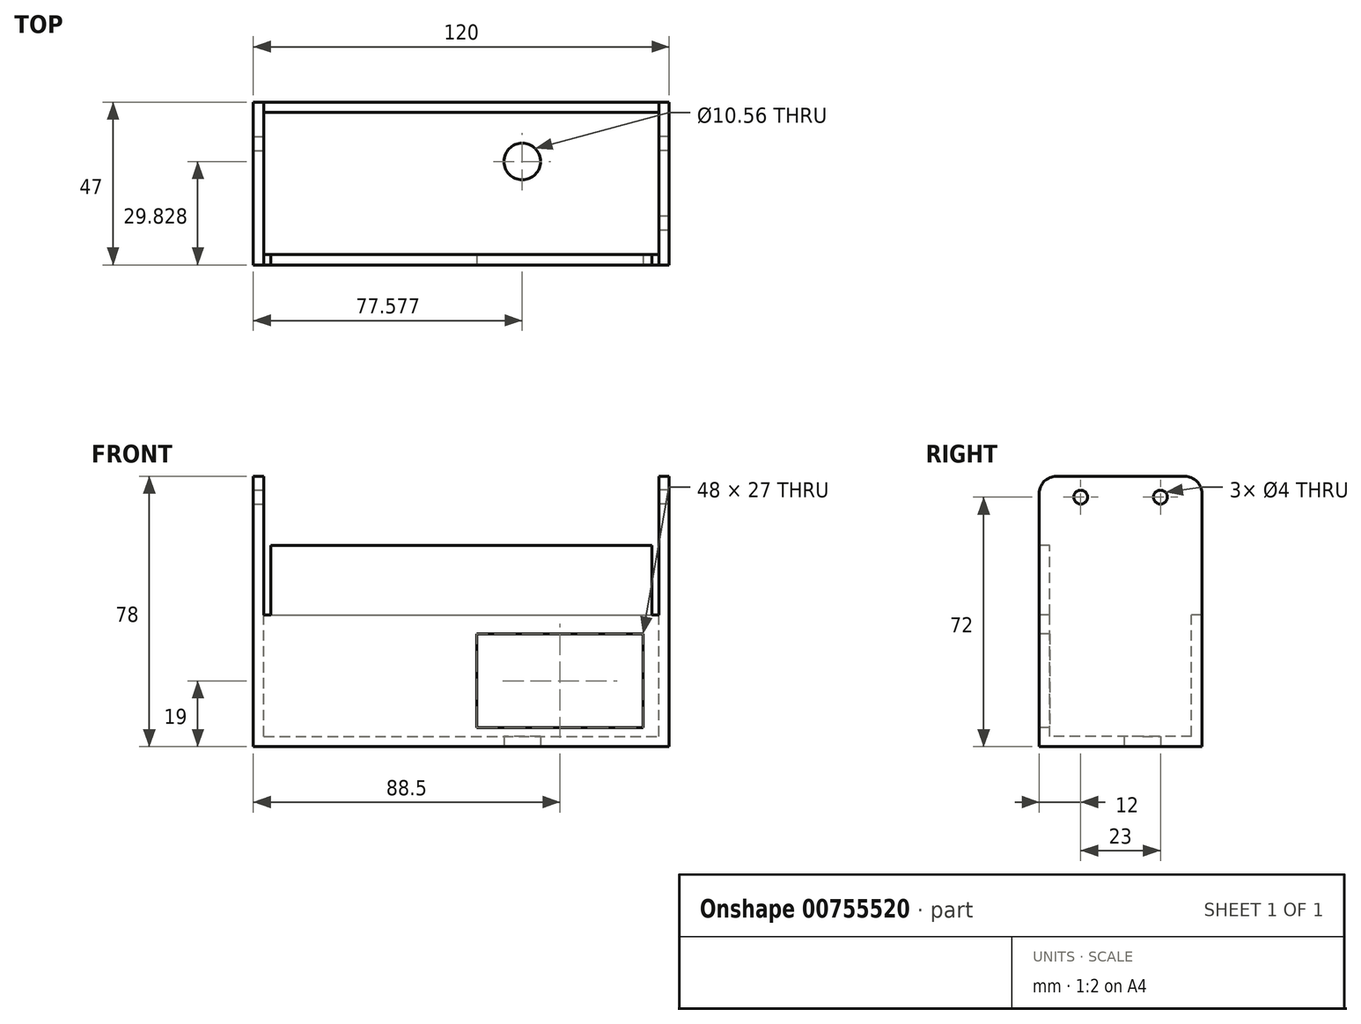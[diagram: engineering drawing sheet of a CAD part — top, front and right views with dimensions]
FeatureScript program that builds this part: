
annotation { "Feature Type Name" : "Feature", "Feature Type Description" : "" }
export const myFeature = defineFeature(function(context is Context, id is Id, definition is map)
    precondition{}
    {
        {
            assignVariable(context, id + "F0", {"name" : "wall", "anyValue" : 3});
        }
        {
            assignVariable(context, id + "F1", {"name" : "width", "anyValue" : 114});
        }
        {
            var Q0;
            Q0=qCreatedBy(makeId("Right.planeOp"),FACE);
            var sketch = newSketch(context, id + "F2", { "sketchPlane" : qUnion([Q0])});
            skLineSegment(sketch, "E0.bottom", {"start": v(17.5, 40) * mm, "end": v(-19.5, 40) * mm});
            skLineSegment(sketch, "E0.top", {"start": v(22.5, -38) * mm, "end": v(-24.5, -38) * mm});
            skLineSegment(sketch, "E0.left", {"start": v(22.5, 35) * mm, "end": v(22.5, -38) * mm});
            skLineSegment(sketch, "E0.right", {"start": v(-24.5, 35) * mm, "end": v(-24.5, -38) * mm});
            skCircle(sketch, "E1", {"center": v(10.5, 34) * mm, "radius": 2 * mm});
            skCircle(sketch, "E2", {"center": v(-12.5, 34) * mm, "radius": 2 * mm});
            skPoint(sketch, "E3.visualSharp", {"position": v(-24.5, 40) * mm});
            skArc(sketch, "E3.filletArc", {"start": v(-19.5, 40) * mm, "mid": v(-23.04, 38.54) * mm, "end": v(-24.5, 35) * mm});
            skPoint(sketch, "E4.visualSharp", {"position": v(22.5, 40) * mm});
            skArc(sketch, "E4.filletArc", {"start": v(22.5, 35) * mm, "mid": v(21.04, 38.54) * mm, "end": v(17.5, 40) * mm});
            skSolve(sketch);
        }
        {
            var Q0;
            Q0=qSketchRegion(id+"F2",true);
            extrude(context, id + "F3", {"entities" : qUnion([Q0]), "depth" : (getVariable(context, 'wall')) * mm, "offsetDistance" : 25 * mm});
        }
        {
            var Q0;
            Q0=qCreatedBy(makeId("Right.planeOp"),FACE);
            var sketch = newSketch(context, id + "F4", { "sketchPlane" : qUnion([Q0])});
            skLineSegment(sketch, "E5.bottom", {"start": v(22.5, -38) * mm, "end": v(-24.5, -38) * mm});
            skLineSegment(sketch, "E5.top", {"start": v(22.5, -35) * mm, "end": v(-24.5, -35) * mm});
            skLineSegment(sketch, "E5.left", {"start": v(22.5, -38) * mm, "end": v(22.5, -35) * mm});
            skLineSegment(sketch, "E5.right", {"start": v(-24.5, -38) * mm, "end": v(-24.5, -35) * mm});
            skLineSegment(sketch, "E6.bottom", {"start": v(-24.5, -38) * mm, "end": v(-21.5, -38) * mm});
            skLineSegment(sketch, "E6.top", {"start": v(-24.5, 0) * mm, "end": v(-21.5, 0) * mm});
            skLineSegment(sketch, "E6.left", {"start": v(-24.5, -38) * mm, "end": v(-24.5, 0) * mm});
            skLineSegment(sketch, "E6.right", {"start": v(-21.5, -38) * mm, "end": v(-21.5, 0) * mm});
            skLineSegment(sketch, "E7.bottom", {"start": v(22.5, -38) * mm, "end": v(19.5, -38) * mm});
            skLineSegment(sketch, "E7.top", {"start": v(22.5, 0) * mm, "end": v(19.5, 0) * mm});
            skLineSegment(sketch, "E7.left", {"start": v(22.5, -38) * mm, "end": v(22.5, 0) * mm});
            skLineSegment(sketch, "E7.right", {"start": v(19.5, -38) * mm, "end": v(19.5, 0) * mm});
            skSolve(sketch);
        }
        {
            var Q0;
            {var subQ0=sQuery(id+"F4.wireOp",EDGE,"E5.right");var subQ1=sQuery(id+"F4.wireOp",EDGE,"E5.bottom");var subQ9=sQuery(id+"F4.wireOp",EDGE,"E7.right");var subQ10=makeQuery(id+"F4.imprint","INTERSECT",VERTEX,{"derivedFrom":[subQ1,subQ9]});var subQ14=sQuery(id+"F4.wireOp",EDGE,"E5.left");var subQ16=sQuery(id+"F4.wireOp",EDGE,"E7.top");var subQ17=sQuery(id+"F4.wireOp",EDGE,"E6.top");Q0=qUnion([makeQuery(id+"F4.imprint","IMPRINT",FACE,{"disambiguationData":[TD([[makeQuery(id+"F4.imprint","IMPRINT",EDGE,{"derivedFrom":subQ17}),-1.0]])]}),makeQuery(id+"F4.imprint","IMPRINT",FACE,{"disambiguationData":[TD([[makeQuery(id+"F4.imprint","IMPRINT",EDGE,{"derivedFrom":subQ14}),1.0]])]}),makeQuery(id+"F4.imprint","IMPRINT",FACE,{"disambiguationData":[TD([[makeQuery(id+"F4.imprint","IMPRINT",EDGE,{"derivedFrom":subQ16}),1.0]])]}),makeQuery(id+"F4.imprint","IMPRINT",FACE,{"disambiguationData":[TD([[makeQuery(id+"F4.imprint","IMPRINT",EDGE,{"disambiguationData":[TD([[subQ10,-1.0]])],"derivedFrom":subQ1}),-1.0]])]}),makeQuery(id+"F4.imprint","IMPRINT",FACE,{"disambiguationData":[TD([[makeQuery(id+"F4.imprint","IMPRINT",EDGE,{"derivedFrom":subQ0}),-1.0]])]})]);}
            extrude(context, id + "F5", {"entities" : qUnion([Q0]), "operationType" : NewBodyOperationType.ADD, "oppositeDirection" : true, "depth" : (getVariable(context, 'width')) * mm, "offsetDistance" : 25 * mm});
        }
        {
            var Q0;
            Q0=makeQuery(id+"F5.opExtrude","CAP_FACE",FACE,{"disambiguationData":[OSD([sQuery(id+"F4.wireOp",EDGE,"E5.bottom"),sQuery(id+"F4.wireOp",EDGE,"E5.top"),sQuery(id+"F4.wireOp",EDGE,"E5.left"),sQuery(id+"F4.wireOp",EDGE,"E5.right"),sQuery(id+"F4.wireOp",EDGE,"E6.top"),sQuery(id+"F4.wireOp",EDGE,"E6.left"),sQuery(id+"F4.wireOp",EDGE,"E6.right"),sQuery(id+"F4.wireOp",EDGE,"E7.top"),sQuery(id+"F4.wireOp",EDGE,"E7.left"),sQuery(id+"F4.wireOp",EDGE,"E7.right")])],"isStart":false});
            var sketch = newSketch(context, id + "F6", { "sketchPlane" : qUnion([Q0])});
            skLineSegment(sketch, "E8.bottom", {"start": v(19.5, 40) * mm, "end": v(-17.5, 40) * mm});
            skLineSegment(sketch, "E8.top", {"start": v(24.5, -38) * mm, "end": v(-22.5, -38) * mm});
            skLineSegment(sketch, "E8.left", {"start": v(24.5, 35) * mm, "end": v(24.5, -38) * mm});
            skLineSegment(sketch, "E8.right", {"start": v(-22.5, 35) * mm, "end": v(-22.5, -38) * mm});
            skCircle(sketch, "E9", {"center": v(-10.5, 34) * mm, "radius": 2 * mm});
            skPoint(sketch, "E10.visualSharp", {"position": v(-22.5, 40) * mm});
            skArc(sketch, "E10.filletArc", {"start": v(-17.5, 40) * mm, "mid": v(-21.04, 38.54) * mm, "end": v(-22.5, 35) * mm});
            skPoint(sketch, "E11.visualSharp", {"position": v(24.5, 40) * mm});
            skArc(sketch, "E11.filletArc", {"start": v(24.5, 35) * mm, "mid": v(23.04, 38.54) * mm, "end": v(19.5, 40) * mm});
            skSolve(sketch);
        }
        {
            var Q0;
            Q0=qSketchRegion(id+"F6",true);
            extrude(context, id + "F7", {"entities" : qUnion([Q0]), "operationType" : NewBodyOperationType.ADD, "depth" : (getVariable(context, 'wall')) * mm, "offsetDistance" : 25 * mm});
        }
        {
            var Q0;
            Q0=makeQuery(id+"F7.boolean.opBoolean","MERGE",FACE,{"derivedFrom":[makeQuery(id+"F5.boolean.opBoolean","MERGE",FACE,{"derivedFrom":[makeQuery(id+"F3.opExtrude","SWEPT_FACE",FACE,{"disambiguationData":[OSD([sQuery(id+"F2.wireOp",EDGE,"E0.right")])]}),makeQuery(id+"F5.opExtrude","SWEPT_FACE",FACE,{"disambiguationData":[OSD([sQuery(id+"F4.wireOp",EDGE,"E5.right"),sQuery(id+"F4.wireOp",EDGE,"E6.left")])]})]}),makeQuery(id+"F7.opExtrude","SWEPT_FACE",FACE,{"disambiguationData":[OSD([sQuery(id+"F6.wireOp",EDGE,"E8.left")])]})]});
            var sketch = newSketch(context, id + "F8", { "sketchPlane" : qUnion([Q0])});
            skLineSegment(sketch, "E12.bottom", {"start": v(-112, 0) * mm, "end": v(-2, 0) * mm});
            skLineSegment(sketch, "E12.top", {"start": v(-112, 20) * mm, "end": v(-2, 20) * mm});
            skLineSegment(sketch, "E12.left", {"start": v(-112, 0) * mm, "end": v(-112, 20) * mm});
            skLineSegment(sketch, "E12.right", {"start": v(-2, 0) * mm, "end": v(-2, 20) * mm});
            skSolve(sketch);
        }
        {
            var Q0;
            Q0=qSketchRegion(id+"F8",true);
            extrude(context, id + "F9", {"entities" : qUnion([Q0]), "operationType" : NewBodyOperationType.ADD, "oppositeDirection" : true, "depth" : (getVariable(context, 'wall')) * mm, "offsetDistance" : 25 * mm});
        }
        {
            var Q0;
            {var subQ2=sQuery(id+"F8.wireOp",EDGE,"E12.bottom");Q0=makeQuery(id+"F8.imprint","IMPRINT",FACE,{"disambiguationData":[TD([[makeQuery(id+"F8.imprint","IMPRINT",EDGE,{"derivedFrom":subQ2}),-1.0]])]});}
            var sketch = newSketch(context, id + "F10", { "sketchPlane" : qUnion([Q0])});
            skLineSegment(sketch, "E13.bottom", {"start": v(-85.5, -19) * mm, "end": v(-85.5, -19) * mm});
            skLineSegment(sketch, "E13.top", {"start": v(-85.5, -19) * mm, "end": v(-85.5, -19) * mm});
            skLineSegment(sketch, "E13.left", {"start": v(-85.5, -19) * mm, "end": v(-85.5, -19) * mm});
            skLineSegment(sketch, "E13.right", {"start": v(-85.5, -19) * mm, "end": v(-85.5, -19) * mm});
            skLineSegment(sketch, "E14.bottom", {"start": v(-52.5, -5.5) * mm, "end": v(-4.5, -5.5) * mm});
            skLineSegment(sketch, "E14.top", {"start": v(-52.5, -32.5) * mm, "end": v(-4.5, -32.5) * mm});
            skLineSegment(sketch, "E14.left", {"start": v(-52.5, -5.5) * mm, "end": v(-52.5, -32.5) * mm});
            skLineSegment(sketch, "E14.right", {"start": v(-4.5, -5.5) * mm, "end": v(-4.5, -32.5) * mm});
            skLineSegment(sketch, "E15", {"start": v(-57, 0) * mm, "end": v(-57, -48.8) * mm, "construction": true});
            skLineSegment(sketch, "E16", {"start": v(-121.46, -19) * mm, "end": v(11.47, -19) * mm, "construction": true});
            skSolve(sketch);
        }
        {
            var Q0;
            Q0=qSketchRegion(id+"F10",true);
            extrude(context, id + "F11", {"entities" : qUnion([Q0]), "operationType" : NewBodyOperationType.REMOVE, "endBound" : BoundingType.UP_TO_NEXT, "oppositeDirection" : true, "depth" : 25 * mm, "offsetDistance" : 25 * mm});
        }
        {
            var Q0;
            Q0=makeQuery(id+"F7.boolean.opBoolean","MERGE",FACE,{"derivedFrom":[makeQuery(id+"F5.boolean.opBoolean","MERGE",FACE,{"derivedFrom":[makeQuery(id+"F3.opExtrude","SWEPT_FACE",FACE,{"disambiguationData":[OSD([sQuery(id+"F2.wireOp",EDGE,"E0.top")])]}),makeQuery(id+"F5.opExtrude","SWEPT_FACE",FACE,{"disambiguationData":[OSD([sQuery(id+"F4.wireOp",EDGE,"E5.bottom")])]})]}),makeQuery(id+"F7.opExtrude","SWEPT_FACE",FACE,{"disambiguationData":[OSD([sQuery(id+"F6.wireOp",EDGE,"E8.top")])]})]});
            var sketch = newSketch(context, id + "F12", { "sketchPlane" : qUnion([Q0])});
            skCircle(sketch, "E17", {"center": v(-39.42, -5.33) * mm, "radius": 5.28 * mm});
            skSolve(sketch);
        }
        {
            var Q0;
            Q0 = qSketchRegion(id + "F12", true);
            extrude(context, id + "F13", {"entities" : qUnion([Q0]), "operationType" : NewBodyOperationType.REMOVE, "endBound" : BoundingType.UP_TO_NEXT, "oppositeDirection" : true, "depth" : 25 * mm, "offsetDistance" : 25 * mm});
        }
    });
